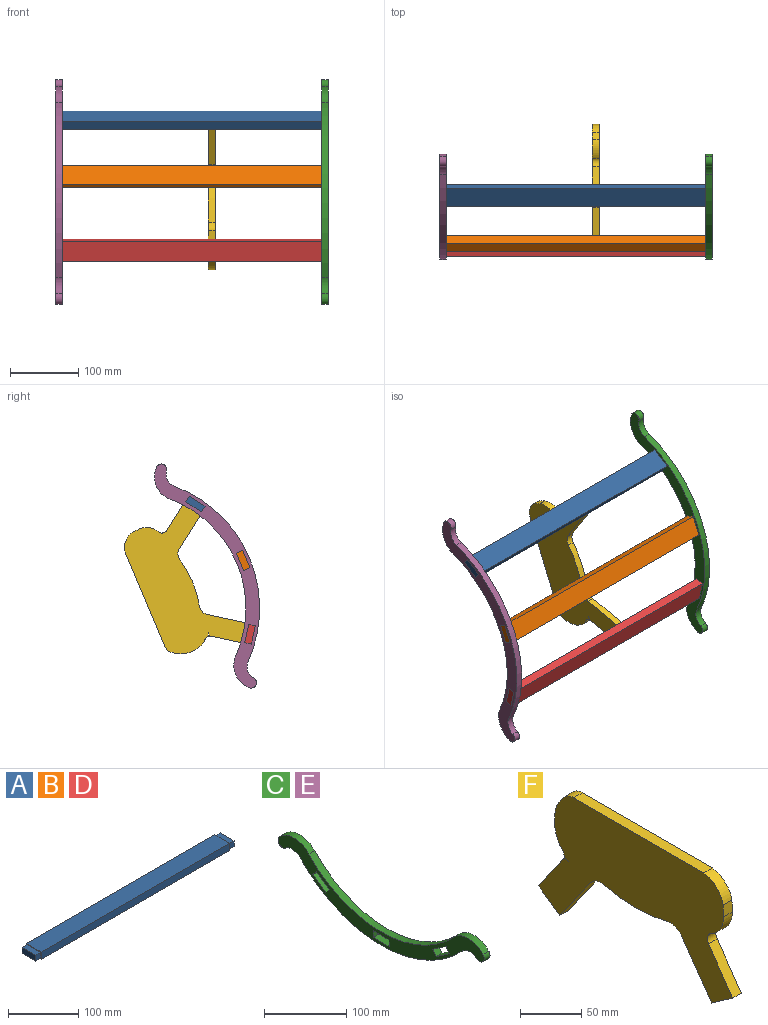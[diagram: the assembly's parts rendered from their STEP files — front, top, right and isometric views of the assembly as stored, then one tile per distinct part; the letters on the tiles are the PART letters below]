
ASSEMBLY  parts=6 mates=12
PART A: 16 faces, bbox 400x30x12.5 mm
  f0: plane 380x12.5mm, normal (0,-1,0), area 4750mm2, adj f1,f3,f8,f14
  f1: plane 380x30mm, normal (0,0,-1), area 11400mm2, adj f0,f2,f8,f14
  f2: plane 380x12.5mm, normal (0,1,0), area 4750mm2, adj f1,f3,f8,f14
  f3: plane 380x30mm, normal (0,0,1), area 11400mm2, adj f0,f2,f8,f14
  f4: plane 27.5x10mm, normal (0,0,-1), area 275mm2, adj f5,f7,f8,f9
  f5: plane 10x10mm, normal (0,-1,0), area 100mm2, adj f4,f6,f8,f9
  f6: plane 27.5x10mm, normal (0,0,1), area 275mm2, adj f5,f7,f8,f9
  f7: plane 10x10mm, normal (0,1,0), area 100mm2, adj f4,f6,f8,f9
  f8: plane 30x12.5mm, normal (1,0,0), area 100mm2, adj f0,f1,f2,f3,f4,f5,f6,f7
  f9: plane 27.5x10mm, normal (1,0,0), area 275mm2, adj f4,f5,f6,f7
  f10: plane 27.5x10mm, normal (0,0,-1), area 275mm2, adj f11,f13,f14,f15
  f11: plane 10x10mm, normal (0,-1,0), area 100mm2, adj f10,f12,f14,f15
  f12: plane 27.5x10mm, normal (0,0,1), area 275mm2, adj f11,f13,f14,f15
  f13: plane 10x10mm, normal (0,1,0), area 100mm2, adj f10,f12,f14,f15
  f14: plane 30x12.5mm, normal (-1,0,0), area 100mm2, adj f0,f1,f2,f3,f10,f11,f12,f13
  f15: plane 27.5x10mm, normal (-1,0,0), area 275mm2, adj f10,f11,f12,f13
PART B: same geometry as A
PART C: 22 faces, bbox 10x355.4x85.1 mm
  f0: plane 355.44x85.12mm, normal (1,0,0), area 6831.3mm2, adj f2,f3,f4,f5,f6,f7,f8,f9
  f1: plane 355.44x85.12mm, normal (-1,0,0), area 6831.3mm2, adj f2,f3,f4,f5,f6,f7,f8,f9
  f2: cylinder r=170.51mm len=249.06mm, axis (-1,0,0), area 2792.3mm2, adj f0,f1,f3,f9
  f3: cylinder r=34.96mm len=51.07mm, axis (-1,0,0), area 572.6mm2, adj f0,f1,f2,f4
  f4: cylinder r=7.85mm len=13.22mm, axis (-1,0,0), area 235.8mm2, adj f0,f1,f3,f5
  f5: cylinder r=18.69mm len=25.43mm, axis (-1,0,0), area 280.6mm2, adj f0,f1,f4,f6
  f6: cylinder r=190.51mm len=278.99mm, axis (-1,0,0), area 3130.3mm2, adj f0,f1,f5,f7
  f7: cylinder r=18.69mm len=25.43mm, axis (-1,0,0), area 280.6mm2, adj f0,f1,f6,f8
  f8: cylinder r=7.85mm len=13.22mm, axis (-1,0,0), area 235.8mm2, adj f0,f1,f7,f9
  f9: cylinder r=34.96mm len=51.07mm, axis (-1,0,0), area 572.6mm2, adj f0,f1,f2,f8
  f10: plane 22.53x15.77mm, normal (0,0.57,-0.82), area 275mm2, adj f0,f1,f11,f13
  f11: plane 10x8.19mm, normal (0,0.82,0.57), area 100mm2, adj f0,f1,f10,f12
  f12: plane 22.53x15.77mm, normal (0,-0.57,0.82), area 275mm2, adj f0,f1,f11,f13
  f13: plane 10x8.19mm, normal (0,-0.82,-0.57), area 100mm2, adj f0,f1,f10,f12
  f14: plane 22.53x15.77mm, normal (0,-0.57,-0.82), area 275mm2, adj f0,f1,f15,f17
  f15: plane 10x8.19mm, normal (0,0.82,-0.57), area 100mm2, adj f0,f1,f14,f16
  f16: plane 22.53x15.77mm, normal (0,0.57,0.82), area 275mm2, adj f0,f1,f15,f17
  f17: plane 10x8.19mm, normal (0,-0.82,0.57), area 100mm2, adj f0,f1,f14,f16
  f18: plane 27.5x10mm, normal (0,0,-1), area 275mm2, adj f0,f1,f19,f21
  f19: plane 10x10mm, normal (0,1,0), area 100mm2, adj f0,f1,f18,f20
  f20: plane 27.5x10mm, normal (0,0,1), area 275mm2, adj f0,f1,f19,f21
  f21: plane 10x10mm, normal (0,-1,0), area 100mm2, adj f0,f1,f18,f20
PART D: same geometry as A
PART E: same geometry as C
PART F: 22 faces, bbox 10x224.5x125.7 mm
  f0: plane 224.48x125.65mm, normal (1,0,0), area 16490.7mm2, adj f2,f3,f4,f5,f6,f7,f8,f9
  f1: plane 224.48x125.65mm, normal (-1,0,0), area 16490.7mm2, adj f2,f3,f4,f5,f6,f7,f8,f9
  f2: cylinder r=323.55mm len=12.03mm, axis (1,0,0), area 120.3mm2, adj f0,f1,f15,f20
  f3: cylinder r=8mm len=10mm, axis (1,0,0), area 25.8mm2, adj f0,f1,f10,f19
  f4: plane 150.43x10mm, normal (0,0,1), area 1504.3mm2, adj f0,f1,f20,f21
  f5: plane 40.12x28.1mm, normal (0,-0.82,0.57), area 489.8mm2, adj f0,f1,f6,f14
  f6: plane 24.57x17.21mm, normal (0,-0.57,-0.82), area 300mm2, adj f0,f1,f5,f7
  f7: plane 50x35.01mm, normal (0,0.82,-0.57), area 610.4mm2, adj f0,f1,f6,f13
  f8: plane 50x35.01mm, normal (0,-0.82,-0.57), area 610.4mm2, adj f0,f1,f9,f12
  f9: plane 24.57x17.21mm, normal (0,0.57,-0.82), area 300mm2, adj f0,f1,f8,f10
  f10: plane 40.12x28.1mm, normal (0,0.82,0.57), area 489.8mm2, adj f0,f1,f3,f9
  f11: cylinder r=152.84mm len=73.52mm, axis (1,0,0), area 742.4mm2, adj f0,f1,f12,f13
  f12: cylinder r=15mm len=15.89mm, axis (1,0,0), area 180.4mm2, adj f0,f1,f8,f11
  f13: cylinder r=15mm len=15.89mm, axis (1,0,0), area 180.4mm2, adj f0,f1,f7,f11
  f14: cylinder r=8mm len=11.71mm, axis (1,0,0), area 136.8mm2, adj f0,f1,f5,f15
  f15: cylinder r=26.51mm len=23.83mm, axis (1,0,0), area 293.5mm2, adj f0,f1,f2,f14
  f16: cylinder r=8mm len=10mm, axis (1,0,0), area 98.8mm2, adj f0,f1,f17,f18
  f17: cylinder r=42.36mm len=51.72mm, axis (1,0,0), area 558.5mm2, adj f0,f1,f16,f21
  f18: plane 10x4.84mm, normal (0,0.35,-0.94), area 51.6mm2, adj f0,f1,f16,f19
  f19: plane 10x5.09mm, normal (0,-0.12,0.99), area 51.3mm2, adj f0,f1,f3,f18
  f20: cylinder r=26.75mm len=22.55mm, axis (1,0,0), area 326.3mm2, adj f0,f1,f2,f4
  f21: cylinder r=15mm len=11.07mm, axis (1,0,0), area 124.6mm2, adj f0,f1,f4,f17
PLACE A rot(axis=(-1,0,0),147.8deg) t=(-99.91,126.94,539.9)mm
PLACE B rot(axis=(1,0,0),67.2deg) t=(-99.91,52.01,449.96)mm
PLACE C rot(axis=(-1,0,0),112.8deg) t=(90.09,74.49,445.34)mm
PLACE D rot(axis=(-1,0,0),77.8deg) t=(-99.91,41.68,350.43)mm
PLACE E rot(axis=(-1,0,0),112.8deg) t=(-299.91,74.49,445.34)mm
PLACE F rot(axis=(-1,0,0),112.8deg) t=(-75.76,118.36,426.88)mm
MATE planar A.f7 <-> C.f17  axis (0,-0.85,-0.53) through (95.09,111.83,529.74)mm
MATE planar D.f15 <-> E.f1  axis (-1,0,0) through (-299.91,43.17,346.19)mm
MATE planar D.f13 <-> E.f13  axis (0,0.21,-0.98) through (-294.91,46.07,332.75)mm
MATE planar D.f3 <-> F.f9  axis (0,0.98,0.21) through (-99.91,49.28,347.51)mm
MATE planar A.f3 <-> F.f6  axis (0,0.53,-0.85) through (-99.91,126.8,531.77)mm
MATE planar D.f9 <-> C.f0  axis (1,0,0) through (100.09,43.17,346.19)mm
MATE planar A.f4 <-> C.f16  axis (0,-0.53,0.85) through (95.09,120.81,541.29)mm
MATE planar A.f9 <-> C.f0  axis (1,0,0) through (100.09,123.47,537.06)mm
MATE planar D.f12 <-> E.f10  axis (0,0.98,0.21) through (-294.91,48.06,347.25)mm
MATE planar D.f7 <-> C.f13  axis (0,0.21,-0.98) through (95.09,46.07,332.75)mm
MATE fastened B.f10 <-> E.f18  axis (0,0.92,-0.39) through (-294.91,57.84,452.35)mm
MATE planar C.f12 <-> D.f4  axis (0,0.98,0.21) through (95.09,38.28,345.13)mm
